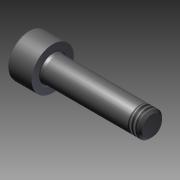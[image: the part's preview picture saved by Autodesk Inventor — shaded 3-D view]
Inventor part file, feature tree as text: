
AUTODESK INVENTOR PART (.ipt)
format: ipt  version: 2011 SP1 (Build 150282100, 282)  size: 134,656 bytes
history: native  units: mm
features: other x28, sketch x2, revolve x1, thread x1, extrude x1
ambient origin geometry x8: Origin, YZ Plane, XZ Plane, XY Plane, X Axis, Y Axis, Z Axis, Center Point
bodies: Solid1 (feature_tree)
feature tree (33):
  revolve  "Revolution1"  [1 undecoded]
  thread  "Thread1"  [1 undecoded]
  extrude  "Extrusion1"  [1 undecoded]
  other  "IP1_XY"
  other  "IP1_YZ"
  other  "IP1_ZX"
  other  "IP1_X"
  other  "IP1_Y"
  other  "IP1_Z"
  other  "IP1_Center"
  other  "IP2_XY"
  other  "IP2_YZ"
  other  "IP2_ZX"
  other  "IP2_X"
  other  "IP2_Y"
  other  "IP2_Z"
  other  "IP2_Center"
  other  "IP3_XY"
  other  "IP3_YZ"
  other  "IP3_ZX"
  other  "IP3_X"
  other  "IP3_Y"
  other  "IP3_Z"
  other  "IP3_Center"
  other  "IP4_XY"
  other  "IP4_YZ"
  other  "IP4_ZX"
  other  "IP4_X"
  other  "IP4_Y"
  other  "IP4_Z"
  other  "IP4_Center"
  sketch  "Skizze_2"  dims[d5=0.0mm d6=0.0mm d7=0.0mm d8=0.0mm]
  sketch  "Skizze_1"  dims[d0=360.0deg d1=1.9095mm d2=0.0mm d3=5.0mm d4=0.0mm]
note: 3 required parameter values undecoded (feature->parameter linkage not recoverable at this tier; creation-order binding heuristic only, values carry confidence <= 0.55)